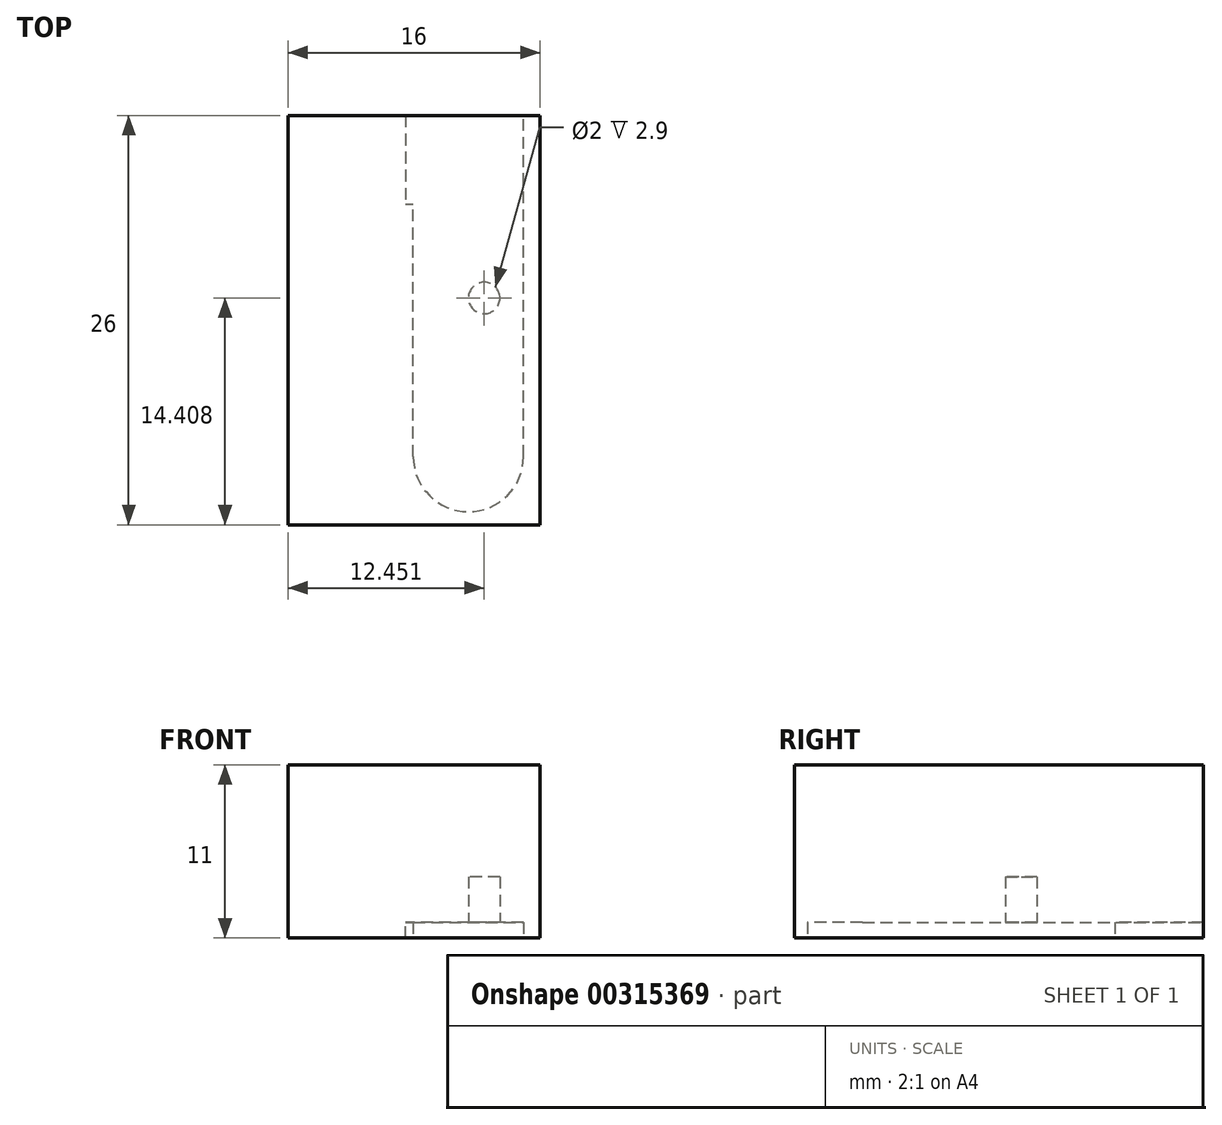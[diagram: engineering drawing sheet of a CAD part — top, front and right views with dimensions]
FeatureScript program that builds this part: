
annotation { "Feature Type Name" : "Feature", "Feature Type Description" : "" }
export const myFeature = defineFeature(function(context is Context, id is Id, definition is map)
    precondition{}
    {
        {
            var Q0;
            Q0=qCreatedBy(makeId("Top.planeOp"),FACE);
            var sketch = newSketch(context, id + "F0", { "sketchPlane" : qUnion([Q0])});
            skLineSegment(sketch, "E0.bottom", {"start": v(8.03, -12.93) * mm, "end": v(-7.97, -12.93) * mm});
            skLineSegment(sketch, "E0.top", {"start": v(8.03, 13.07) * mm, "end": v(4.13, 13.07) * mm});
            skLineSegment(sketch, "E0.left", {"start": v(8.03, -12.93) * mm, "end": v(8.03, 13.07) * mm});
            skLineSegment(sketch, "E0.right", {"start": v(-7.97, -12.93) * mm, "end": v(-7.97, 13.07) * mm});
            skPoint(sketch, "E1.orphan", {"position": v(9.28, -8.97) * mm});
            skLineSegment(sketch, "E2.trimOffspring", {"start": v(0.03, 13.07) * mm, "end": v(-7.97, 13.07) * mm});
            skPoint(sketch, "E3.left.start.orphan", {"position": v(7.08, -12.43) * mm});
            skLineSegment(sketch, "E4", {"start": v(0.03, 13.07) * mm, "end": v(4.13, 13.07) * mm});
            skSolve(sketch);
        }
        {
            var Q0;
            Q0=makeQuery(id+"F0.imprint","IMPRINT",FACE,{"disambiguationData":[TD([[makeQuery(id+"F0.imprint","IMPRINT",EDGE,{"derivedFrom":sQuery(id+"F0.wireOp",EDGE,"E0.bottom")}),-1.0]])]});
            extrude(context, id + "F1", {"entities" : qUnion([Q0]), "depth" : 11 * mm});
        }
        {
            var Q0;
            Q0=qCreatedBy(makeId("Top.planeOp"),FACE);
            var sketch = newSketch(context, id + "F2", { "sketchPlane" : qUnion([Q0])});
            skPoint(sketch, "E5.middle", {"position": v(-0.03, 0.73) * mm});
            skLineSegment(sketch, "E6.top", {"start": v(4.34, 2.47) * mm, "end": v(4.63, 2.47) * mm, "construction": true});
            skArc(sketch, "E7", {"start": v(-0.02, -8.6) * mm, "mid": v(3.48, -12.1) * mm, "end": v(6.98, -8.6) * mm});
            skLineSegment(sketch, "E8", {"start": v(-0.02, -8.6) * mm, "end": v(-0.02, 7.44) * mm});
            skLineSegment(sketch, "E9", {"start": v(6.98, -8.6) * mm, "end": v(6.98, 15.1) * mm});
            skPoint(sketch, "E10.orphan", {"position": v(6.98, 15.1) * mm});
            skCircle(sketch, "E11", {"center": v(4.48, 1.48) * mm, "radius": 1 * mm});
            skPoint(sketch, "E12.endSnap0", {"position": v(-0.02, 3.15) * mm});
            skLineSegment(sketch, "E13.top", {"start": v(-0.52, 7.44) * mm, "end": v(-0.02, 7.44) * mm});
            skLineSegment(sketch, "E13.left", {"start": v(-0.52, 14.27) * mm, "end": v(-0.52, 7.44) * mm});
            skLineSegment(sketch, "E14", {"start": v(6.98, 15.1) * mm, "end": v(-0.52, 14.27) * mm});
            skSolve(sketch);
        }
        {
            var Q0;
            Q0=makeQuery(id+"F2.imprint","IMPRINT",FACE,{"disambiguationData":[TD([[makeQuery(id+"F2.imprint","IMPRINT",EDGE,{"derivedFrom":sQuery(id+"F2.wireOp",EDGE,"E7")}),1.0]])]});
            var Q1;
            Q1=makeQuery(id+"F2.imprint","IMPRINT",FACE,{"disambiguationData":[TD([[makeQuery(id+"F2.imprint","IMPRINT",EDGE,{"derivedFrom":sQuery(id+"F2.wireOp",EDGE,"E11")}),1.0]])]});
            extrude(context, id + "F3", {"entities" : qUnion([Q0, Q1]), "operationType" : NewBodyOperationType.REMOVE, "depth" : 1 * mm});
        }
        {
            var Q0;
            Q0=makeQuery(id+"F2.imprint","IMPRINT",FACE,{"disambiguationData":[TD([[makeQuery(id+"F2.imprint","IMPRINT",EDGE,{"derivedFrom":sQuery(id+"F2.wireOp",EDGE,"E11")}),1.0]])]});
            extrude(context, id + "F4", {"entities" : qUnion([Q0]), "operationType" : NewBodyOperationType.REMOVE, "depth" : 3.9 * mm});
        }
    });
